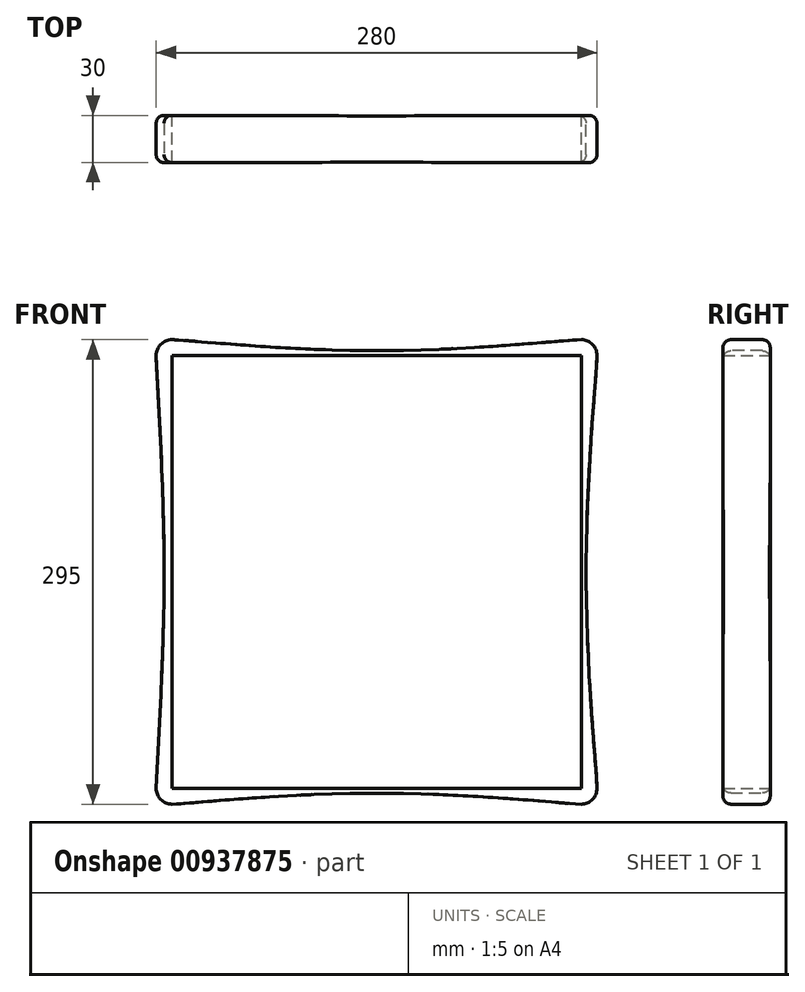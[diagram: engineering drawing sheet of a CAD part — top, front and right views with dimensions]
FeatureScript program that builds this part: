
annotation { "Feature Type Name" : "Feature", "Feature Type Description" : "" }
export const myFeature = defineFeature(function(context is Context, id is Id, definition is map)
    precondition{}
    {
        {
            var Q0;
            Q0=qCreatedBy(makeId("Front.planeOp"),FACE);
            var sketch = newSketch(context, id + "F0", { "sketchPlane" : qUnion([Q0])});
            skLineSegment(sketch, "E0.bottom", {"start": v(130, 137.5) * mm, "end": v(-130, 137.5) * mm});
            skLineSegment(sketch, "E0.top", {"start": v(130, -137.5) * mm, "end": v(-130, -137.5) * mm});
            skLineSegment(sketch, "E0.left", {"start": v(130, 137.5) * mm, "end": v(130, -137.5) * mm});
            skLineSegment(sketch, "E0.right", {"start": v(-130, 137.5) * mm, "end": v(-130, -137.5) * mm});
            skPoint(sketch, "E0.middle", {"position": v(0, 0) * mm});
            skCircle(sketch, "E1", {"center": v(-130, 137.5) * mm, "radius": 10 * mm});
            skCircle(sketch, "E2", {"center": v(130, 137.5) * mm, "radius": 10 * mm});
            skCircle(sketch, "E3", {"center": v(-130, -137.5) * mm, "radius": 10 * mm});
            skCircle(sketch, "E4", {"center": v(130, -137.5) * mm, "radius": 10 * mm});
            skPoint(sketch, "E5", {"position": v(-120, 137.5) * mm});
            skPoint(sketch, "E6", {"position": v(120, 137.5) * mm});
            skPoint(sketch, "E7", {"position": v(130, 127.5) * mm});
            skPoint(sketch, "E8", {"position": v(130, -127.5) * mm});
            skPoint(sketch, "E9", {"position": v(120, -137.5) * mm});
            skPoint(sketch, "E10", {"position": v(-120, -137.5) * mm});
            skPoint(sketch, "E11", {"position": v(-130, -127.5) * mm});
            skPoint(sketch, "E12", {"position": v(-130, 127.5) * mm});
            skPoint(sketch, "E13", {"position": v(0, 140.5) * mm});
            skPoint(sketch, "E14", {"position": v(133, 0) * mm});
            skPoint(sketch, "E15", {"position": v(0, -140.5) * mm});
            skPoint(sketch, "E16", {"position": v(-135, 0) * mm});
            skFitSpline(sketch, "E17", {"points": [v(130, 147.5) * mm, v(0, 140.5) * mm, v(-130, 147.5) * mm], "startDerivative": vector(-60, 0) * mm, "endDerivative": vector(-60, 0) * mm});
            skFitSpline(sketch, "E18", {"points": [v(140, 137.5) * mm, v(133, 0) * mm, v(140, -137.5) * mm], "startDerivative": vector(0, -60) * mm, "endDerivative": vector(0, -60) * mm});
            skFitSpline(sketch, "E19", {"points": [v(130, -147.5) * mm, v(0, -140.5) * mm, v(-130, -147.5) * mm], "startDerivative": vector(-60, 0) * mm, "endDerivative": vector(-60, 0) * mm});
            skFitSpline(sketch, "E20", {"points": [v(-140, 137.5) * mm, v(-135, 0) * mm, v(-140, -137.5) * mm], "startDerivative": vector(0, -60) * mm, "endDerivative": vector(0, -60) * mm});
            skSolve(sketch);
        }
        {
            var Q0;
            {var subQ5=sQuery(id+"F0.wireOp",EDGE,"E17");Q0=makeQuery(id+"F0.imprint","IMPRINT",FACE,{"disambiguationData":[TD([[makeQuery(id+"F0.imprint","IMPRINT",EDGE,{"derivedFrom":subQ5}),1.0]])]});}
            var Q1;
            {var subQ3=sQuery(id+"F0.wireOp",EDGE,"E0.right");var subQ4=sQuery(id+"F0.wireOp",EDGE,"E0.bottom");var subQ5=makeQuery(id+"F0.imprint","INTERSECT",VERTEX,{"derivedFrom":[subQ4,subQ3]});Q1=makeQuery(id+"F0.imprint","IMPRINT",FACE,{"disambiguationData":[TD([[makeQuery(id+"F0.imprint","IMPRINT",EDGE,{"disambiguationData":[TD([[subQ5,1.0]])],"derivedFrom":subQ4}),-1.0]])]});}
            var Q2;
            {var subQ5=sQuery(id+"F0.wireOp",EDGE,"E20");Q2=makeQuery(id+"F0.imprint","IMPRINT",FACE,{"disambiguationData":[TD([[makeQuery(id+"F0.imprint","IMPRINT",EDGE,{"derivedFrom":subQ5}),1.0]])]});}
            var Q3;
            {var subQ3=sQuery(id+"F0.wireOp",EDGE,"E0.right");var subQ4=sQuery(id+"F0.wireOp",EDGE,"E0.top");var subQ5=makeQuery(id+"F0.imprint","INTERSECT",VERTEX,{"derivedFrom":[subQ4,subQ3]});Q3=makeQuery(id+"F0.imprint","IMPRINT",FACE,{"disambiguationData":[TD([[makeQuery(id+"F0.imprint","IMPRINT",EDGE,{"disambiguationData":[TD([[subQ5,1.0]])],"derivedFrom":subQ4}),1.0]])]});}
            var Q4;
            {var subQ5=sQuery(id+"F0.wireOp",EDGE,"E19");Q4=makeQuery(id+"F0.imprint","IMPRINT",FACE,{"disambiguationData":[TD([[makeQuery(id+"F0.imprint","IMPRINT",EDGE,{"derivedFrom":subQ5}),-1.0]])]});}
            var Q5;
            {var subQ2=sQuery(id+"F0.wireOp",EDGE,"E0.top");var subQ5=sQuery(id+"F0.wireOp",EDGE,"E0.left");var subQ7=makeQuery(id+"F0.imprint","INTERSECT",VERTEX,{"derivedFrom":[subQ2,subQ5]});Q5=makeQuery(id+"F0.imprint","IMPRINT",FACE,{"disambiguationData":[TD([[makeQuery(id+"F0.imprint","IMPRINT",EDGE,{"disambiguationData":[TD([[subQ7,-1.0]])],"derivedFrom":subQ2}),1.0]])]});}
            var Q6;
            {var subQ5=sQuery(id+"F0.wireOp",EDGE,"E18");Q6=makeQuery(id+"F0.imprint","IMPRINT",FACE,{"disambiguationData":[TD([[makeQuery(id+"F0.imprint","IMPRINT",EDGE,{"derivedFrom":subQ5}),-1.0]])]});}
            var Q7;
            {var subQ2=sQuery(id+"F0.wireOp",EDGE,"E0.bottom");var subQ4=sQuery(id+"F0.wireOp",EDGE,"E0.left");var subQ5=makeQuery(id+"F0.imprint","INTERSECT",VERTEX,{"derivedFrom":[subQ2,subQ4]});Q7=makeQuery(id+"F0.imprint","IMPRINT",FACE,{"disambiguationData":[TD([[makeQuery(id+"F0.imprint","IMPRINT",EDGE,{"disambiguationData":[TD([[subQ5,-1.0]])],"derivedFrom":subQ2}),-1.0]])]});}
            extrude(context, id + "F1", {"entities" : qUnion([Q0, Q1, Q2, Q3, Q4, Q5, Q6, Q7]), "endBound" : BoundingType.SYMMETRIC, "depth" : 30 * mm, "offsetDistance" : 25 * mm});
        }
        {
            var Q0;
            Q0=makeQuery(id+"F1.opExtrude","CAP_EDGE",EDGE,{"disambiguationData":[OSD([sQuery(id+"F0.wireOp",EDGE,"E17")])],"isStart":true});
            var Q1;
            Q1=makeQuery(id+"F1.opExtrude","CAP_EDGE",EDGE,{"disambiguationData":[OSD([sQuery(id+"F0.wireOp",EDGE,"E17")])],"isStart":false});
            fillet(context, id + "F2", {"entities" : qUnion([Q0, Q1]), "radius" : 5 * mm, "tangentPropagation" : true, "allowEdgeOverflow" : false});
        }
    });
